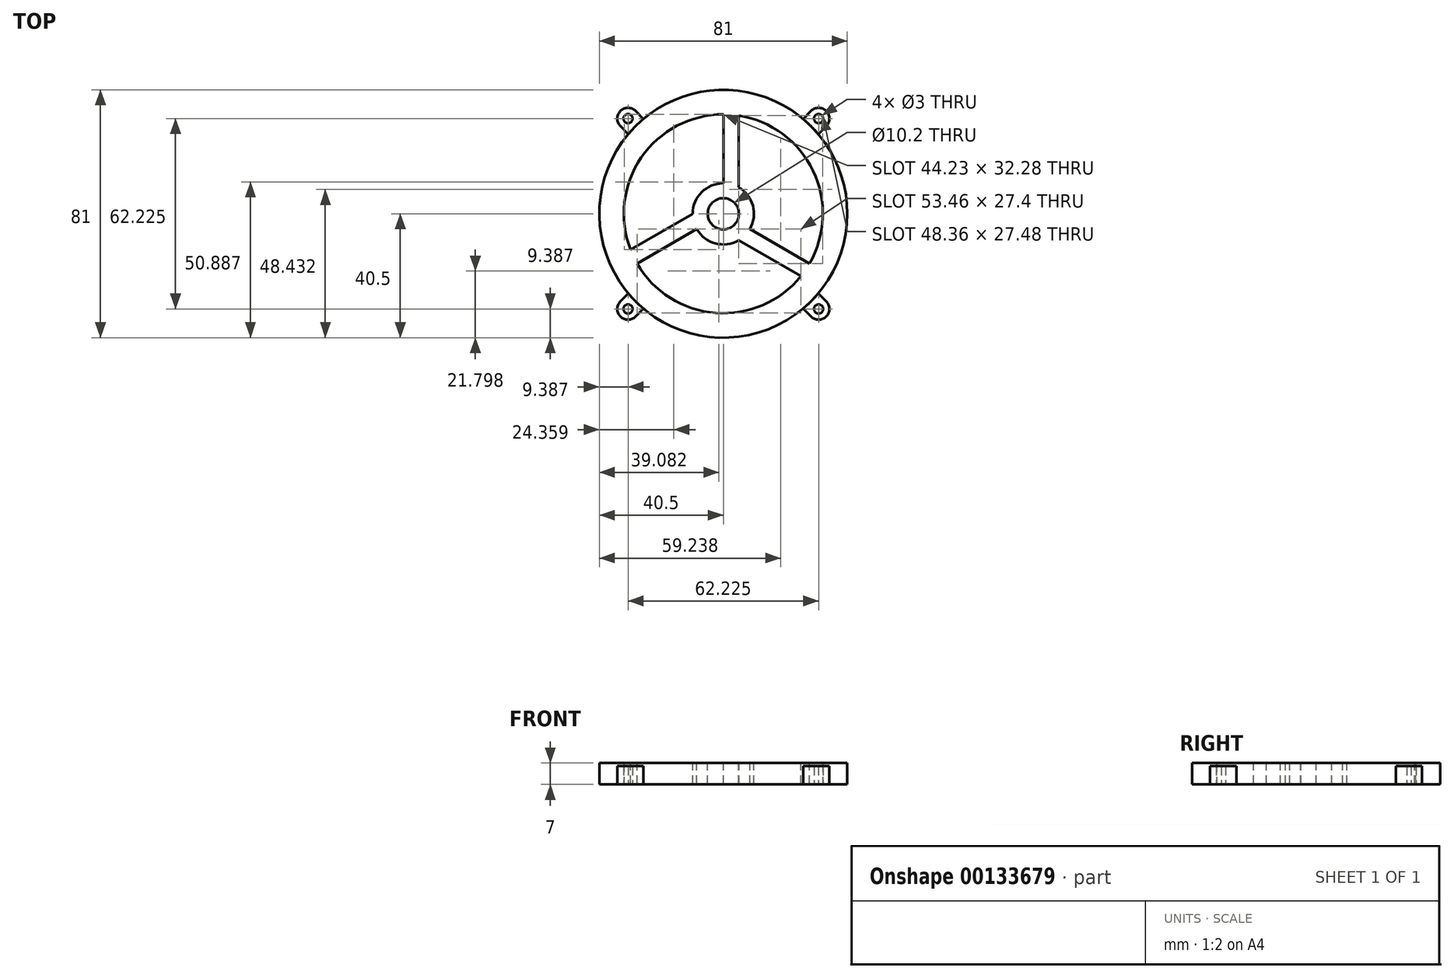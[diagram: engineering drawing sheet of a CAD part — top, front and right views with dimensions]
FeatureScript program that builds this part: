
annotation { "Feature Type Name" : "Feature", "Feature Type Description" : "" }
export const myFeature = defineFeature(function(context is Context, id is Id, definition is map)
    precondition{}
    {
        {
            var Q0;
            Q0=qCreatedBy(makeId("Top.planeOp"),FACE);
            var sketch = newSketch(context, id + "F0", { "sketchPlane" : qUnion([Q0])});
            skCircle(sketch, "E0", {"center": v(0, 0) * mm, "radius": 37 * mm});
            skCircle(sketch, "E1", {"center": v(0, 0) * mm, "radius": 32.5 * mm});
            skCircle(sketch, "E2", {"center": v(0, 0) * mm, "radius": 40.5 * mm});
            skLineSegment(sketch, "E3", {"start": v(0, 0) * mm, "end": v(-31.11, 31.11) * mm, "construction": true});
            skCircle(sketch, "E4", {"center": v(-31.11, 31.11) * mm, "radius": 1.5 * mm});
            skArc(sketch, "E5", {"start": v(-28.64, 33.59) * mm, "mid": v(-33.59, 33.59) * mm, "end": v(-33.59, 28.64) * mm});
            skLineSegment(sketch, "E6", {"start": v(-33.59, 28.64) * mm, "end": v(-31, 26.06) * mm});
            skLineSegment(sketch, "E7", {"start": v(-28.64, 33.59) * mm, "end": v(-26.06, 31) * mm});
            skLineSegment(sketch, "E8.1.0", {"start": v(-33.59, -28.64) * mm, "end": v(-31, -26.06) * mm});
            skCircle(sketch, "E8.1.1", {"center": v(-31.11, -31.11) * mm, "radius": 1.5 * mm});
            skArc(sketch, "E8.1.2", {"start": v(-33.59, -28.64) * mm, "mid": v(-33.59, -33.59) * mm, "end": v(-28.64, -33.59) * mm});
            skLineSegment(sketch, "E8.1.3", {"start": v(-28.64, -33.59) * mm, "end": v(-26.06, -31) * mm});
            skLineSegment(sketch, "E8.2.0", {"start": v(28.64, -33.59) * mm, "end": v(26.06, -31) * mm});
            skCircle(sketch, "E8.2.1", {"center": v(31.11, -31.11) * mm, "radius": 1.5 * mm});
            skArc(sketch, "E8.2.2", {"start": v(28.64, -33.59) * mm, "mid": v(33.59, -33.59) * mm, "end": v(33.59, -28.64) * mm});
            skLineSegment(sketch, "E8.2.3", {"start": v(33.59, -28.64) * mm, "end": v(31, -26.06) * mm});
            skLineSegment(sketch, "E8.3.0", {"start": v(33.59, 28.64) * mm, "end": v(31, 26.06) * mm});
            skCircle(sketch, "E8.3.1", {"center": v(31.11, 31.11) * mm, "radius": 1.5 * mm});
            skArc(sketch, "E8.3.2", {"start": v(33.59, 28.64) * mm, "mid": v(33.59, 33.59) * mm, "end": v(28.64, 33.59) * mm});
            skLineSegment(sketch, "E8.3.3", {"start": v(28.64, 33.59) * mm, "end": v(26.06, 31) * mm});
            skLineSegment(sketch, "E9", {"start": v(0, 0) * mm, "end": v(0, 25.38) * mm, "construction": true});
            skSolve(sketch);
        }
        {
            var Q0;
            Q0=makeQuery(id+"F0.imprint","IMPRINT",FACE,{"disambiguationData":[TD([[makeQuery(id+"F0.imprint","IMPRINT",EDGE,{"derivedFrom":sQuery(id+"F0.wireOp",EDGE,"E0")}),-1.0]])]});
            extrude(context, id + "F1", {"entities" : qUnion([Q0]), "depth" : 7 * mm});
        }
        {
            var Q0;
            {var subQ0=sQuery(id+"F0.wireOp",EDGE,"E8.1.0");Q0=makeQuery(id+"F0.imprint","IMPRINT",FACE,{"disambiguationData":[TD([[makeQuery(id+"F0.imprint","IMPRINT",EDGE,{"derivedFrom":subQ0}),-1.0]])]});}
            var Q1;
            {var subQ1=sQuery(id+"F0.wireOp",EDGE,"E8.2.0");Q1=makeQuery(id+"F0.imprint","IMPRINT",FACE,{"disambiguationData":[TD([[makeQuery(id+"F0.imprint","IMPRINT",EDGE,{"derivedFrom":subQ1}),-1.0]])]});}
            var Q2;
            {var subQ0=sQuery(id+"F0.wireOp",EDGE,"E8.3.0");Q2=makeQuery(id+"F0.imprint","IMPRINT",FACE,{"disambiguationData":[TD([[makeQuery(id+"F0.imprint","IMPRINT",EDGE,{"derivedFrom":subQ0}),-1.0]])]});}
            var Q3;
            Q3=makeQuery(id+"F0.imprint","IMPRINT",FACE,{"disambiguationData":[TD([[makeQuery(id+"F0.imprint","IMPRINT",EDGE,{"derivedFrom":sQuery(id+"F0.wireOp",EDGE,"E4")}),-1.0]])]});
            extrude(context, id + "F2", {"entities" : qUnion([Q0, Q1, Q2, Q3]), "operationType" : NewBodyOperationType.ADD, "depth" : 6 * mm});
        }
        {
            var Q0;
            Q0=makeQuery(id+"F0.imprint","IMPRINT",FACE,{"disambiguationData":[TD([[makeQuery(id+"F0.imprint","IMPRINT",EDGE,{"derivedFrom":sQuery(id+"F0.wireOp",EDGE,"E0")}),1.0]])]});
            extrude(context, id + "F3", {"entities" : qUnion([Q0]), "operationType" : NewBodyOperationType.ADD, "depth" : 7 * mm});
        }
        {
            var Q0;
            Q0=makeQuery(id+"F3.opExtrude","CAP_FACE",FACE,{"disambiguationData":[OSD([sQuery(id+"F0.wireOp",EDGE,"E0"),sQuery(id+"F0.wireOp",EDGE,"E1")])],"isStart":false});
            var sketch = newSketch(context, id + "F4", { "sketchPlane" : qUnion([Q0])});
            skCircle(sketch, "E10", {"center": v(0, 0) * mm, "radius": 5.1 * mm});
            skCircle(sketch, "E11", {"center": v(0, 0) * mm, "radius": 10 * mm});
            skLineSegment(sketch, "E12", {"start": v(0, 0) * mm, "end": v(0, 32.5) * mm});
            skLineSegment(sketch, "E13.1.0", {"start": v(0, 0) * mm, "end": v(-28.15, -16.25) * mm});
            skLineSegment(sketch, "E13.2.0", {"start": v(0, 0) * mm, "end": v(28.15, -16.25) * mm});
            skLineSegment(sketch, "E14.0", {"start": v(5, 0) * mm, "end": v(5, 32.5) * mm});
            skLineSegment(sketch, "E15.0", {"start": v(-2.5, -4.33) * mm, "end": v(25.65, -20.58) * mm});
            skLineSegment(sketch, "E16.0", {"start": v(-2.5, 4.33) * mm, "end": v(-30.65, -11.92) * mm});
            skSolve(sketch);
        }
        {
            var Q0;
            {var subQ0=sQuery(id+"F4.wireOp",EDGE,"E12");var subQ1=sQuery(id+"F4.wireOp",EDGE,"E11");var subQ2=makeQuery(id+"F4.imprint","INTERSECT",VERTEX,{"derivedFrom":[subQ1,subQ0]});Q0=makeQuery(id+"F4.imprint","IMPRINT",FACE,{"disambiguationData":[TD([[makeQuery(id+"F4.imprint","IMPRINT",EDGE,{"disambiguationData":[TD([[subQ2,1.0]])],"derivedFrom":subQ1}),-1.0]])]});}
            var Q1;
            {var subQ0=sQuery(id+"F4.wireOp",EDGE,"E14.0");var subQ1=sQuery(id+"F4.wireOp",EDGE,"E10");var subQ2=makeQuery(id+"F4.imprint","INTERSECT",VERTEX,{"derivedFrom":[subQ1,subQ0]});Q1=makeQuery(id+"F4.imprint","IMPRINT",FACE,{"disambiguationData":[TD([[makeQuery(id+"F4.imprint","IMPRINT",EDGE,{"disambiguationData":[TD([[subQ2,1.0]])],"derivedFrom":subQ1}),-1.0]])]});}
            var Q2;
            {var subQ0=sQuery(id+"F4.wireOp",EDGE,"E14.0");var subQ1=sQuery(id+"F4.wireOp",EDGE,"E10");var subQ2=makeQuery(id+"F4.imprint","INTERSECT",VERTEX,{"derivedFrom":[subQ1,subQ0]});Q2=makeQuery(id+"F4.imprint","IMPRINT",FACE,{"disambiguationData":[TD([[makeQuery(id+"F4.imprint","IMPRINT",EDGE,{"disambiguationData":[TD([[subQ2,-1.0]])],"derivedFrom":subQ1}),-1.0]])]});}
            var Q3;
            {var subQ0=sQuery(id+"F4.wireOp",EDGE,"E16.0");var subQ1=sQuery(id+"F4.wireOp",EDGE,"E10");var subQ2=makeQuery(id+"F4.imprint","INTERSECT",VERTEX,{"derivedFrom":[subQ1,subQ0]});Q3=makeQuery(id+"F4.imprint","IMPRINT",FACE,{"disambiguationData":[TD([[makeQuery(id+"F4.imprint","IMPRINT",EDGE,{"disambiguationData":[TD([[subQ2,1.0]])],"derivedFrom":subQ1}),-1.0]])]});}
            var Q4;
            {var subQ0=sQuery(id+"F4.wireOp",EDGE,"E16.0");var subQ1=sQuery(id+"F4.wireOp",EDGE,"E10");var subQ2=makeQuery(id+"F4.imprint","INTERSECT",VERTEX,{"derivedFrom":[subQ1,subQ0]});Q4=makeQuery(id+"F4.imprint","IMPRINT",FACE,{"disambiguationData":[TD([[makeQuery(id+"F4.imprint","IMPRINT",EDGE,{"disambiguationData":[TD([[subQ2,-1.0]])],"derivedFrom":subQ1}),-1.0]])]});}
            var Q5;
            {var subQ0=sQuery(id+"F4.wireOp",EDGE,"E15.0");var subQ1=sQuery(id+"F4.wireOp",EDGE,"E10");var subQ2=makeQuery(id+"F4.imprint","INTERSECT",VERTEX,{"derivedFrom":[subQ1,subQ0]});Q5=makeQuery(id+"F4.imprint","IMPRINT",FACE,{"disambiguationData":[TD([[makeQuery(id+"F4.imprint","IMPRINT",EDGE,{"disambiguationData":[TD([[subQ2,1.0]])],"derivedFrom":subQ1}),-1.0]])]});}
            var Q6;
            {var subQ0=sQuery(id+"F4.wireOp",EDGE,"E15.0");var subQ1=sQuery(id+"F4.wireOp",EDGE,"E10");var subQ2=makeQuery(id+"F4.imprint","INTERSECT",VERTEX,{"derivedFrom":[subQ1,subQ0]});Q6=makeQuery(id+"F4.imprint","IMPRINT",FACE,{"disambiguationData":[TD([[makeQuery(id+"F4.imprint","IMPRINT",EDGE,{"disambiguationData":[TD([[subQ2,-1.0]])],"derivedFrom":subQ1}),-1.0]])]});}
            var Q7;
            {var subQ0=sQuery(id+"F4.wireOp",EDGE,"E15.0");var subQ1=sQuery(id+"F4.wireOp",EDGE,"E11");var subQ2=makeQuery(id+"F4.imprint","INTERSECT",VERTEX,{"derivedFrom":[subQ1,subQ0]});Q7=makeQuery(id+"F4.imprint","IMPRINT",FACE,{"disambiguationData":[TD([[makeQuery(id+"F4.imprint","IMPRINT",EDGE,{"disambiguationData":[TD([[subQ2,-1.0]])],"derivedFrom":subQ1}),-1.0]])]});}
            var Q8;
            {var subQ0=sQuery(id+"F4.wireOp",EDGE,"E16.0");var subQ1=sQuery(id+"F4.wireOp",EDGE,"E11");var subQ2=makeQuery(id+"F4.imprint","INTERSECT",VERTEX,{"derivedFrom":[subQ1,subQ0]});Q8=makeQuery(id+"F4.imprint","IMPRINT",FACE,{"disambiguationData":[TD([[makeQuery(id+"F4.imprint","IMPRINT",EDGE,{"disambiguationData":[TD([[subQ2,-1.0]])],"derivedFrom":subQ1}),-1.0]])]});}
            extrude(context, id + "F5", {"entities" : qUnion([Q0, Q1, Q2, Q3, Q4, Q5, Q6, Q7, Q8]), "operationType" : NewBodyOperationType.ADD, "oppositeDirection" : true, "depth" : 7 * mm});
        }
    });
